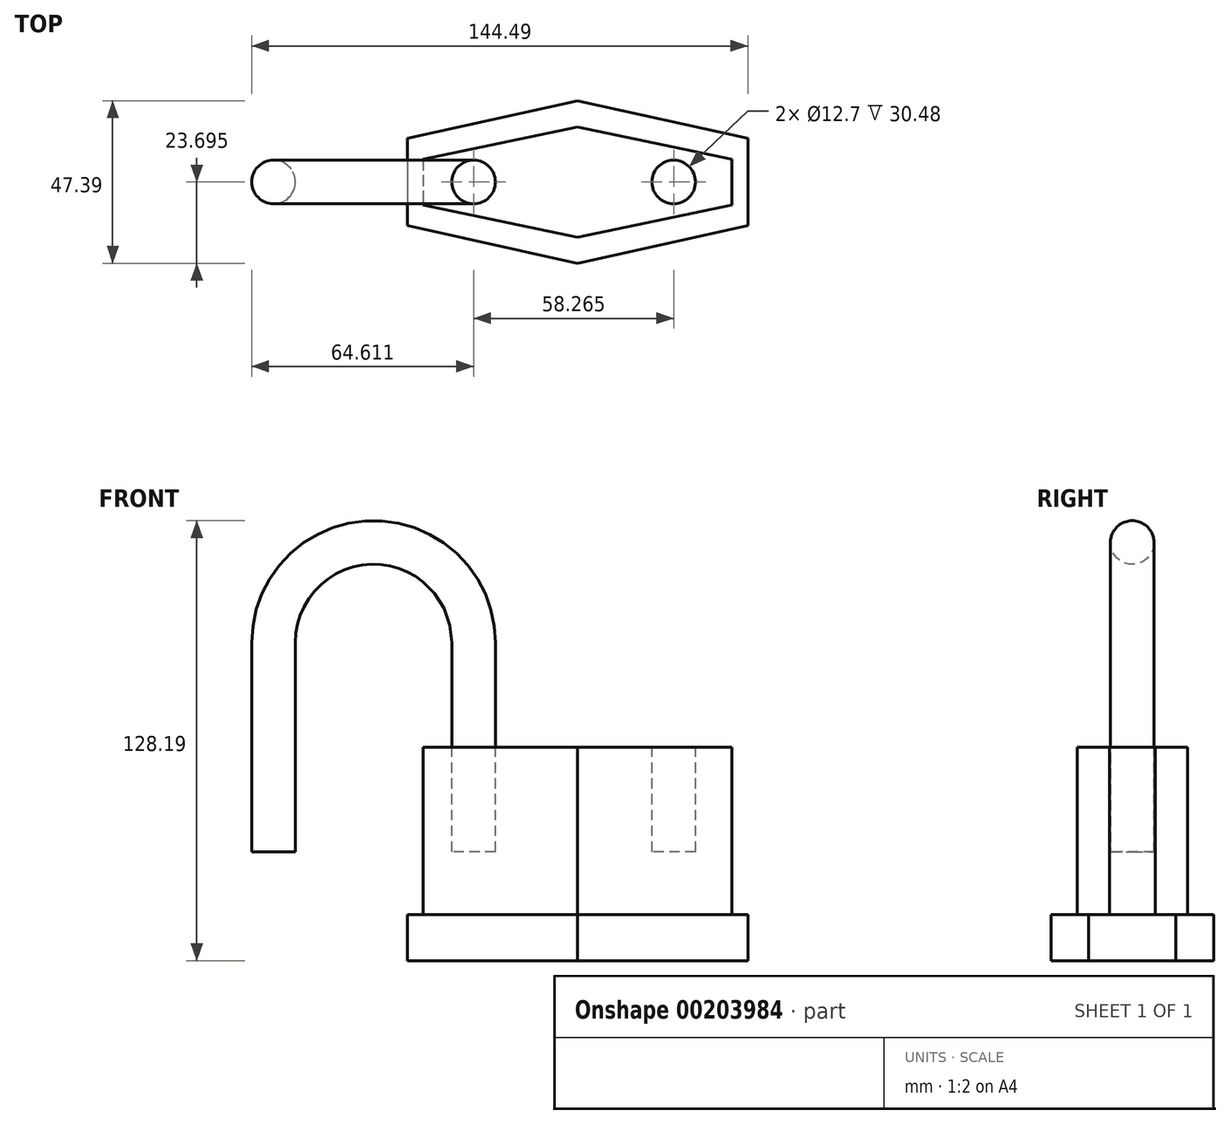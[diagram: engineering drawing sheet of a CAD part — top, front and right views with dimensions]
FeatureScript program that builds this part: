
annotation { "Feature Type Name" : "Feature", "Feature Type Description" : "" }
export const myFeature = defineFeature(function(context is Context, id is Id, definition is map)
    precondition{}
    {
        {
            var Q0;
            Q0=qCreatedBy(makeId("Top.planeOp"),FACE);
            var sketch = newSketch(context, id + "F0", { "sketchPlane" : qUnion([Q0])});
            skLineSegment(sketch, "E0", {"start": v(-59.37, 19.38) * mm, "end": v(-59.37, -6.02) * mm});
            skLineSegment(sketch, "E1", {"start": v(-59.37, -6.02) * mm, "end": v(-9.78, -17.02) * mm});
            skLineSegment(sketch, "E2", {"start": v(-9.78, -17.02) * mm, "end": v(39.82, -6.02) * mm});
            skLineSegment(sketch, "E3", {"start": v(39.82, -6.02) * mm, "end": v(39.82, 19.38) * mm});
            skLineSegment(sketch, "E4", {"start": v(39.82, 19.38) * mm, "end": v(-9.78, 30.37) * mm});
            skLineSegment(sketch, "E5", {"start": v(-9.78, 30.37) * mm, "end": v(-59.37, 19.38) * mm});
            skLineSegment(sketch, "E6", {"start": v(-9.78, 73.4) * mm, "end": v(-9.78, -30.23) * mm, "construction": true});
            skSolve(sketch);
        }
        {
            var Q0;
            Q0=makeQuery(id+"F0.imprint","IMPRINT",FACE,{"disambiguationData":[TD([[makeQuery(id+"F0.imprint","IMPRINT",EDGE,{"derivedFrom":sQuery(id+"F0.wireOp",EDGE,"E0")}),1.0]])]});
            extrude(context, id + "F1", {"entities" : qUnion([Q0]), "depth" : 13.46 * mm});
        }
        {
            var Q0;
            Q0=makeQuery(id+"F1.opExtrude","CAP_FACE",FACE,{"disambiguationData":[OSD([sQuery(id+"F0.wireOp",EDGE,"E0"),sQuery(id+"F0.wireOp",EDGE,"E1"),sQuery(id+"F0.wireOp",EDGE,"E2"),sQuery(id+"F0.wireOp",EDGE,"E3"),sQuery(id+"F0.wireOp",EDGE,"E4"),sQuery(id+"F0.wireOp",EDGE,"E5")])],"isStart":false});
            var sketch = newSketch(context, id + "F2", { "sketchPlane" : qUnion([Q0])});
            skLineSegment(sketch, "E7", {"start": v(-54.7, 13.35) * mm, "end": v(-54.7, 0) * mm});
            skLineSegment(sketch, "E8", {"start": v(-54.7, 0) * mm, "end": v(-9.78, -9.4) * mm});
            skLineSegment(sketch, "E9", {"start": v(-9.78, -9.4) * mm, "end": v(35.15, 0) * mm});
            skLineSegment(sketch, "E10", {"start": v(35.15, 0) * mm, "end": v(35.15, 13.35) * mm});
            skLineSegment(sketch, "E11", {"start": v(35.15, 13.35) * mm, "end": v(-9.78, 22.75) * mm});
            skLineSegment(sketch, "E12", {"start": v(-9.78, 22.75) * mm, "end": v(-54.7, 13.35) * mm});
            skSolve(sketch);
        }
        {
            var Q0;
            Q0=makeQuery(id+"F2.imprint","IMPRINT",FACE,{"disambiguationData":[TD([[makeQuery(id+"F2.imprint","IMPRINT",EDGE,{"derivedFrom":sQuery(id+"F2.wireOp",EDGE,"E7")}),1.0]])]});
            extrude(context, id + "F3", {"entities" : qUnion([Q0]), "operationType" : NewBodyOperationType.ADD, "depth" : 48.77 * mm});
        }
        {
            var Q0;
            Q0=makeQuery(id+"F3.opExtrude","CAP_FACE",FACE,{"disambiguationData":[OSD([sQuery(id+"F2.wireOp",EDGE,"E7"),sQuery(id+"F2.wireOp",EDGE,"E8"),sQuery(id+"F2.wireOp",EDGE,"E9"),sQuery(id+"F2.wireOp",EDGE,"E10"),sQuery(id+"F2.wireOp",EDGE,"E11"),sQuery(id+"F2.wireOp",EDGE,"E12")])],"isStart":false});
            var sketch = newSketch(context, id + "F4", { "sketchPlane" : qUnion([Q0])});
            skCircle(sketch, "E13", {"center": v(18.2, 6.68) * mm, "radius": 6.35 * mm});
            skPoint(sketch, "E13.centerSnap0", {"position": v(-54.7, 6.68) * mm});
            skCircle(sketch, "E14", {"center": v(-40.06, 6.68) * mm, "radius": 6.35 * mm});
            skSolve(sketch);
        }
        {
            var Q0;
            Q0=makeQuery(id+"F4.imprint","IMPRINT",FACE,{"disambiguationData":[TD([[makeQuery(id+"F4.imprint","IMPRINT",EDGE,{"derivedFrom":sQuery(id+"F4.wireOp",EDGE,"E13")}),1.0]])]});
            var Q1;
            Q1=sQuery(id+"F4.wireOp",EDGE,"E13");
            extrude(context, id + "F5", {"entities" : qUnion([Q0]), "operationType" : NewBodyOperationType.REMOVE, "surfaceEntities" : qUnion([Q1]), "oppositeDirection" : true, "depth" : 30.48 * mm});
        }
        {
            assignVariable(context, id + "F6", {"name" : "x", "anyValue" : 30.48 * mm});
        }
        {
            var Q0;
            Q0=qCreatedBy(makeId("Front.planeOp"),FACE);
            var sketch = newSketch(context, id + "F7", { "sketchPlane" : qUnion([Q0])});
            skLineSegment(sketch, "E15", {"start": v(-40.06, 62.23) * mm, "end": v(-40.06, 92.71) * mm});
            skArc(sketch, "E16", {"start": v(-40.06, 92.71) * mm, "mid": v(-69.2, 121.84) * mm, "end": v(-98.32, 92.7) * mm});
            skLineSegment(sketch, "E17", {"start": v(-98.32, 92.7) * mm, "end": v(-40.06, 92.7) * mm, "construction": true});
            skLineSegment(sketch, "E18", {"start": v(-98.32, 92.7) * mm, "end": v(-98.32, 31.75) * mm});
            skSolve(sketch);
        }
        {
            var Q0;
            Q0=makeQuery(id+"F4.imprint","IMPRINT",FACE,{"disambiguationData":[TD([[makeQuery(id+"F4.imprint","IMPRINT",EDGE,{"derivedFrom":sQuery(id+"F4.wireOp",EDGE,"E14")}),1.0]])]});
            var Q1;
            Q1=sQuery(id+"F4.wireOp",EDGE,"E14");
            var Q2;
            Q2=sQuery(id+"F7.wireOp",EDGE,"E15");
            var Q3;
            Q3=sQuery(id+"F7.wireOp",EDGE,"E16");
            var Q4;
            Q4=sQuery(id+"F7.wireOp",EDGE,"E18");
            sweep(context, id + "F8", {"profiles" : qUnion([Q0]), "surfaceProfiles" : qUnion([Q1]), "path" : qUnion([Q2, Q3, Q4])});
        }
        {
            var Q0;
            Q0=makeQuery(id+"F3.opExtrude","CAP_FACE",FACE,{"disambiguationData":[OSD([sQuery(id+"F2.wireOp",EDGE,"E7"),sQuery(id+"F2.wireOp",EDGE,"E8"),sQuery(id+"F2.wireOp",EDGE,"E9"),sQuery(id+"F2.wireOp",EDGE,"E10"),sQuery(id+"F2.wireOp",EDGE,"E11"),sQuery(id+"F2.wireOp",EDGE,"E12")])],"isStart":false});
            var sketch = newSketch(context, id + "F9", { "sketchPlane" : qUnion([Q0])});
            skCircle(sketch, "E19", {"center": v(-40.06, 6.68) * mm, "radius": 6.35 * mm});
            skSolve(sketch);
        }
        {
            var Q0;
            Q0 = qSketchRegion(id + "F9", true);
            extrude(context, id + "F10", {"entities" : qUnion([Q0]), "operationType" : NewBodyOperationType.REMOVE, "oppositeDirection" : true, "depth" : getVariable(context, 'x')});
        }
    });
